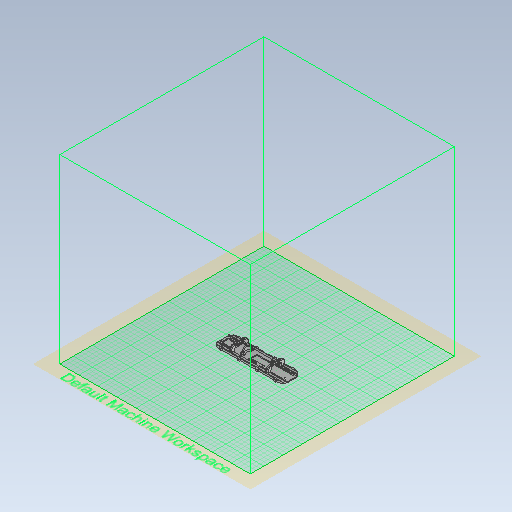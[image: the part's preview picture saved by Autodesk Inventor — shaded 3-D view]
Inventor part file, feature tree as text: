
AUTODESK INVENTOR PART (.ipt)
format: ipt  version: 2021 (Build 250183000, 183)  size: 3,139,072 bytes
history: native  units: in
note: dims shown in document units (in); Inventor stores cm internally (conversion verified against a paired STEP export)
features: extrude x15, sketch x15, fillet x13, mirror x10, plane x3, chamfer x3
ambient origin geometry x8: Origin, YZ Plane, XZ Plane, XY Plane, X Axis, Y Axis, Z Axis, Center Point
bodies: Solid1 (feature_tree)
feature tree (59):
  extrude  "Extrusion1"  Depth=4.9606in
  extrude  "Extrusion2"  TaperAngle=0.0deg  [1 undecoded]
  plane  "Work Plane1"
  plane  "Work Plane2"
  extrude  "Extrusion5"  Depth=0.2362in
  fillet  "Fillet2"  Radius=0.0787in
  mirror  "Mirror3"
  extrude  "Extrusion6"  TaperAngle=0.0deg  [1 undecoded]
  extrude  "Extrusion7"  Depth=0.2362in
  extrude  "Extrusion9"  [1 undecoded]
  extrude  "Extrusion10"  Depth=0.5354in
  fillet  "Fillet4"  Radius=0.9449in
  mirror  "Mirror4"
  mirror  "Mirror5"
  fillet  "Fillet5"  Radius=2.7559in
  fillet  "Fillet6"  Radius=0.4724in
  extrude  "Extrusion12"  Depth=0.0866in TaperAngle=0.0deg
  extrude  "Extrusion13"  Depth=0.0945in
  mirror  "Mirror8"
  mirror  "Mirror9"
  mirror  "Mirror10"
  fillet  "Fillet9"  Radius=0.0945in
  fillet  "Fillet11"  Radius=0.0945in
  fillet  "Fillet12"  [1 undecoded]
  extrude  "Extrusion17"  TaperAngle=0.0deg  [1 undecoded]
  fillet  "Fillet16"  [1 undecoded]
  mirror  "Mirror13"
  extrude  "Extrusion22"  Depth=1.8in
  chamfer  "Chamfer5"  Distance=0.1575in
  fillet  "Fillet29"  Radius=1.9685in
  fillet  "Fillet30"  Radius=0.9449in
  fillet  "Fillet31"  Radius=0.4724in
  extrude  "Extrusion11"  Depth=0.0945in
  plane  "Work Plane4"
  sketch  "Sketch52"  dims[d47=0.35in d48=0.1575in d49=0.0in d60=1.9685in d61=0.9449in d62=0.4724in]
  extrude  "Extrusion24"  Depth=0.0945in
  chamfer  "Chamfer7"  [1 undecoded]
  extrude  "Extrusion25"  TaperAngle=0.0deg  [1 undecoded]
  extrude  "Extrusion26"  TaperAngle=0.0deg  [1 undecoded]
  fillet  "Fillet32"  [1 undecoded]
  mirror  "Mirror19"
  mirror  "Mirror20"
  mirror  "Mirror21"
  fillet  "Fillet33"  Radius=0.9in
  chamfer  "Chamfer9"  Distance=0.7in
  sketch  "Sketch1"  dims[d0=0.1575in d1=0.0in d2=4.9606in]
  sketch  "Sketch2"  dims[d3=1.5512in d4=0.0in]
  sketch  "Sketch7"  dims[d5=0.0in d6=0.2362in d7=0.0787in d8=0.0in]
  sketch  "Sketch8"  dims[d15=-0.7756in d16=0.0in]
  sketch  "Sketch13"  dims[d17=0.0in d18=0.2362in]
  sketch  "Sketch14"  dims[d19=1.3386in d24=-2.4803in]
  sketch  "Sketch15"  dims[d28=0.5354in d29=0.0in d30=0.5354in d31=0.9449in d32=2.7559in d33=0.4724in]
  sketch  "Sketch25"  dims[d34=0.811in d35=0.0866in d36=0.0in]
  sketch  "Sketch27"  dims[d37=0.0945in d38=0.0945in d39=0.0945in d40=0.0945in d41=0.0in]
  sketch  "Sketch39"  dims[d42=0.0in d43=0.0in d44=0.0in]
  sketch  "Sketch49"  dims[d45=0.7in d46=1.8in]
  sketch  "Sketch53"  dims[d63=1.7087in d64=0.0945in]
  sketch  "Sketch54"  dims[d65=0.0945in d66=0.0945in]
  sketch  "Sketch55"  dims[d67=0.0945in d68=0.0in d69=0.0in d70=0.0in d71=0.0in d72=0.9in d73=0.7in d74=0.35in d75=0.1969in d79=0.4094in d80=0.0in d81=0.0in d82=0.0in d83=0.0in d84=0.0in d85=0.0787in d86=0.0in d88=0.3543in d89=0.315in d92=0.0394in d93=0.0in d96=1.1024in d97=0.5512in d98=0.2756in d99=0.0787in d116=0.2362in d117=0.0in d118=0.0in d119=0.1181in d120=0.0394in d121=0.0in d126=0.126in d127=1.5748in d128=0.0in d131=0.0394in d133=0.0551in d134=0.0in d138=0.5709in d148=0.0591in d171=0.0866in d172=0.0394in d173=0.0394in d174=0.0866in d175=0.2638in d176=0.0866in d177=0.0945in d178=0.0866in d179=0.0394in d180=0.0394in d181=0.0787in d182=0.0236in d183=0.0in d184=0.0433in d204=0.0945in d240=0.0in d243=0.0in d244=0.0in d245=0.0in d246=0.1575in d247=0.1575in d248=0.315in d249=0.4724in d250=0.0in d263=0.8661in d264=0.4331in d265=0.7087in d266=0.3543in d267=0.1181in d268=0.315in d269=45.0deg d275=0.0591in d276=0.0394in d277=0.0787in d278=4.7244in d279=0.0in d285=0.0in d286=0.0in d288=-1.5748in d289=0.3937in d291=0.1969in d292=0.0787in d293=0.0in d298=0.0787in d299=0.1496in d300=45.0deg d301=0.3937in d302=0.0in d303=0.0823in d304=0.077in d305=0.126in d306=0.0in d307=0.0in d308=0.0886in d309=0.1516in d310=0.4252in d311=0.1575in d315=0.1575in d316=0.063in d317=45.0deg d146=0.0197in d147=0.0344in d149=0.0344in d211=0.0197in d212=0.0344in d213=0.0197in d214=0.0344in d287=0.0197in]
note: 10 required parameter values undecoded (feature->parameter linkage not recoverable at this tier; creation-order binding heuristic only, values carry confidence <= 0.55)
